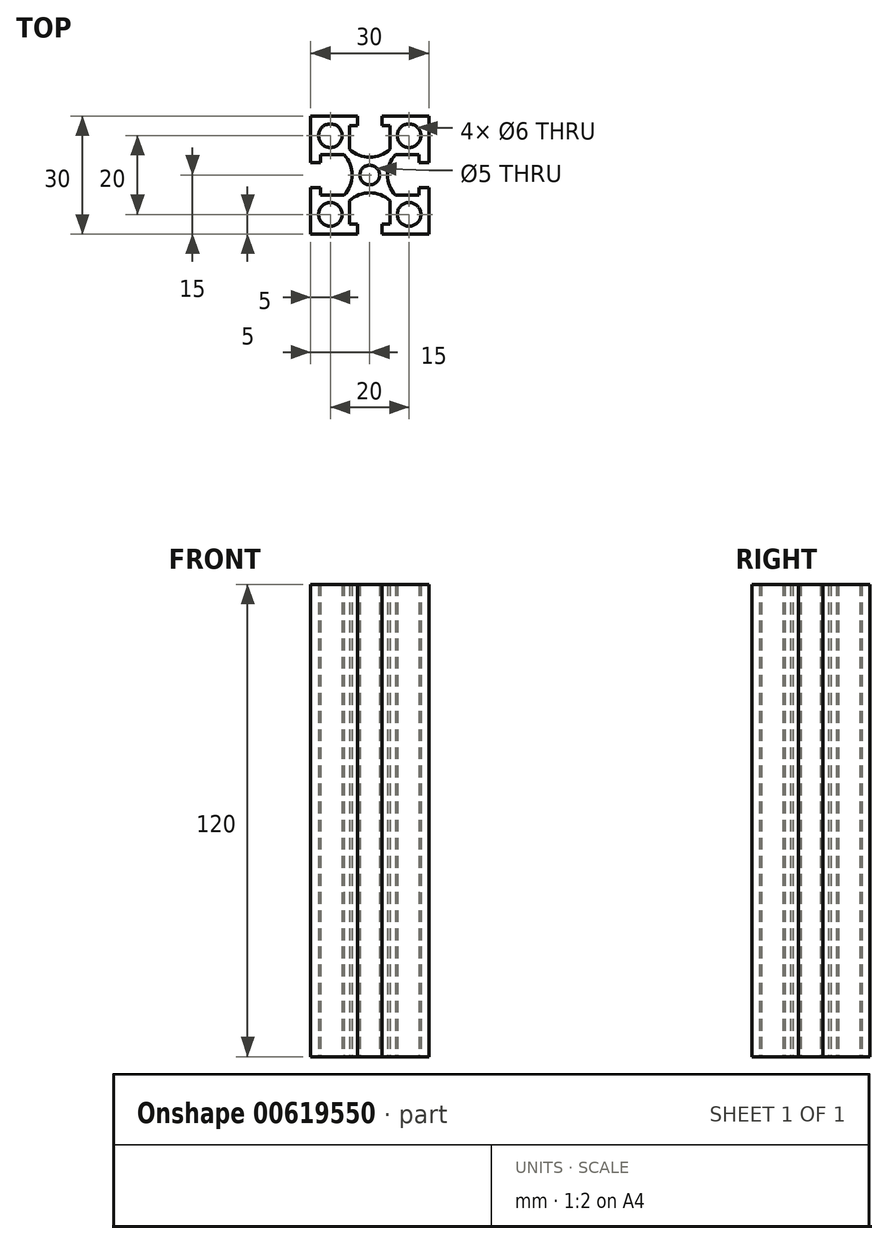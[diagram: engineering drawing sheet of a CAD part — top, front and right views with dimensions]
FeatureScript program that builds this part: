
annotation { "Feature Type Name" : "Feature", "Feature Type Description" : "" }
export const myFeature = defineFeature(function(context is Context, id is Id, definition is map)
    precondition{}
    {
        {
            var Q0;
            Q0=qCreatedBy(makeId("Top.planeOp"),FACE);
            var sketch = newSketch(context, id + "F0", { "sketchPlane" : qUnion([Q0])});
            skCircle(sketch, "E0", {"center": v(-10, 10) * mm, "radius": 3 * mm});
            skCircle(sketch, "E1.MirrorC", {"center": v(-10, -10) * mm, "radius": 3 * mm});
            skLineSegment(sketch, "E2.top", {"start": v(-15, 3.15) * mm, "end": v(-15, -3.15) * mm});
            skLineSegment(sketch, "E2.left", {"start": v(-12.5, 3.15) * mm, "end": v(-15, 3.15) * mm});
            skLineSegment(sketch, "E2.right", {"start": v(-12.5, -3.15) * mm, "end": v(-15, -3.15) * mm});
            skLineSegment(sketch, "E3.bottom", {"start": v(-12.5, 5.15) * mm, "end": v(-12.5, 3.15) * mm});
            skLineSegment(sketch, "E3.left", {"start": v(-12.5, 5.15) * mm, "end": v(-6.55, 5.15) * mm});
            skLineSegment(sketch, "E3.right", {"start": v(-12.5, -5.15) * mm, "end": v(-6.55, -5.15) * mm});
            skArc(sketch, "E4", {"start": v(-6.55, -5.15) * mm, "mid": v(-4.5, 0) * mm, "end": v(-6.55, 5.15) * mm});
            skLineSegment(sketch, "E5.trimOffspring", {"start": v(-12.5, -3.15) * mm, "end": v(-12.5, -5.15) * mm});
            skLineSegment(sketch, "E6.bottom", {"start": v(15, -15) * mm, "end": v(-15, -15) * mm});
            skLineSegment(sketch, "E6.top", {"start": v(15, 15) * mm, "end": v(-15, 15) * mm});
            skLineSegment(sketch, "E6.left", {"start": v(15, -15) * mm, "end": v(15, 15) * mm});
            skLineSegment(sketch, "E6.right", {"start": v(-15, -15) * mm, "end": v(-15, 15) * mm});
            skPoint(sketch, "E6.middle", {"position": v(0, 0) * mm});
            skCircle(sketch, "E7.MirrorC", {"center": v(10, 10) * mm, "radius": 3 * mm});
            skCircle(sketch, "E8.MirrorC", {"center": v(10, -10) * mm, "radius": 3 * mm});
            skLineSegment(sketch, "E9.1.0", {"start": v(-5.15, -12.5) * mm, "end": v(-3.15, -12.5) * mm});
            skArc(sketch, "E9.1.1", {"start": v(5.15, -6.55) * mm, "mid": v(0, -4.5) * mm, "end": v(-5.15, -6.55) * mm});
            skLineSegment(sketch, "E9.1.2", {"start": v(-3.15, -15) * mm, "end": v(3.15, -15) * mm});
            skLineSegment(sketch, "E9.1.3", {"start": v(-3.15, -12.5) * mm, "end": v(-3.15, -15) * mm});
            skLineSegment(sketch, "E9.1.4", {"start": v(-5.15, -12.5) * mm, "end": v(-5.15, -6.55) * mm});
            skLineSegment(sketch, "E9.1.5", {"start": v(3.15, -12.5) * mm, "end": v(5.15, -12.5) * mm});
            skLineSegment(sketch, "E9.1.6", {"start": v(5.15, -12.5) * mm, "end": v(5.15, -6.55) * mm});
            skLineSegment(sketch, "E9.1.7", {"start": v(3.15, -12.5) * mm, "end": v(3.15, -15) * mm});
            skLineSegment(sketch, "E9.2.0", {"start": v(12.5, -5.15) * mm, "end": v(12.5, -3.15) * mm});
            skArc(sketch, "E9.2.1", {"start": v(6.55, 5.15) * mm, "mid": v(4.5, 0) * mm, "end": v(6.55, -5.15) * mm});
            skLineSegment(sketch, "E9.2.2", {"start": v(15, -3.15) * mm, "end": v(15, 3.15) * mm});
            skLineSegment(sketch, "E9.2.3", {"start": v(12.5, -3.15) * mm, "end": v(15, -3.15) * mm});
            skLineSegment(sketch, "E9.2.4", {"start": v(12.5, -5.15) * mm, "end": v(6.55, -5.15) * mm});
            skLineSegment(sketch, "E9.2.5", {"start": v(12.5, 3.15) * mm, "end": v(12.5, 5.15) * mm});
            skLineSegment(sketch, "E9.2.6", {"start": v(12.5, 5.15) * mm, "end": v(6.55, 5.15) * mm});
            skLineSegment(sketch, "E9.2.7", {"start": v(12.5, 3.15) * mm, "end": v(15, 3.15) * mm});
            skLineSegment(sketch, "E9.3.0", {"start": v(5.15, 12.5) * mm, "end": v(3.15, 12.5) * mm});
            skArc(sketch, "E9.3.1", {"start": v(-5.15, 6.55) * mm, "mid": v(0, 4.5) * mm, "end": v(5.15, 6.55) * mm});
            skLineSegment(sketch, "E9.3.2", {"start": v(3.15, 15) * mm, "end": v(-3.15, 15) * mm});
            skLineSegment(sketch, "E9.3.3", {"start": v(3.15, 12.5) * mm, "end": v(3.15, 15) * mm});
            skLineSegment(sketch, "E9.3.4", {"start": v(5.15, 12.5) * mm, "end": v(5.15, 6.55) * mm});
            skLineSegment(sketch, "E9.3.5", {"start": v(-3.15, 12.5) * mm, "end": v(-5.15, 12.5) * mm});
            skLineSegment(sketch, "E9.3.6", {"start": v(-5.15, 12.5) * mm, "end": v(-5.15, 6.55) * mm});
            skLineSegment(sketch, "E9.3.7", {"start": v(-3.15, 12.5) * mm, "end": v(-3.15, 15) * mm});
            skCircle(sketch, "E10", {"center": v(0, 0) * mm, "radius": 2.5 * mm});
            skSolve(sketch);
        }
        {
            var Q0;
            Q0=makeQuery(id+"F0.imprint","IMPRINT",FACE,{"disambiguationData":[TD([[makeQuery(id+"F0.imprint","IMPRINT",EDGE,{"derivedFrom":sQuery(id+"F0.wireOp",EDGE,"E0")}),-1.0]])]});
            extrude(context, id + "F1", {"entities" : qUnion([Q0]), "depth" : 120 * mm, "offsetDistance" : 25 * mm});
        }
    });
